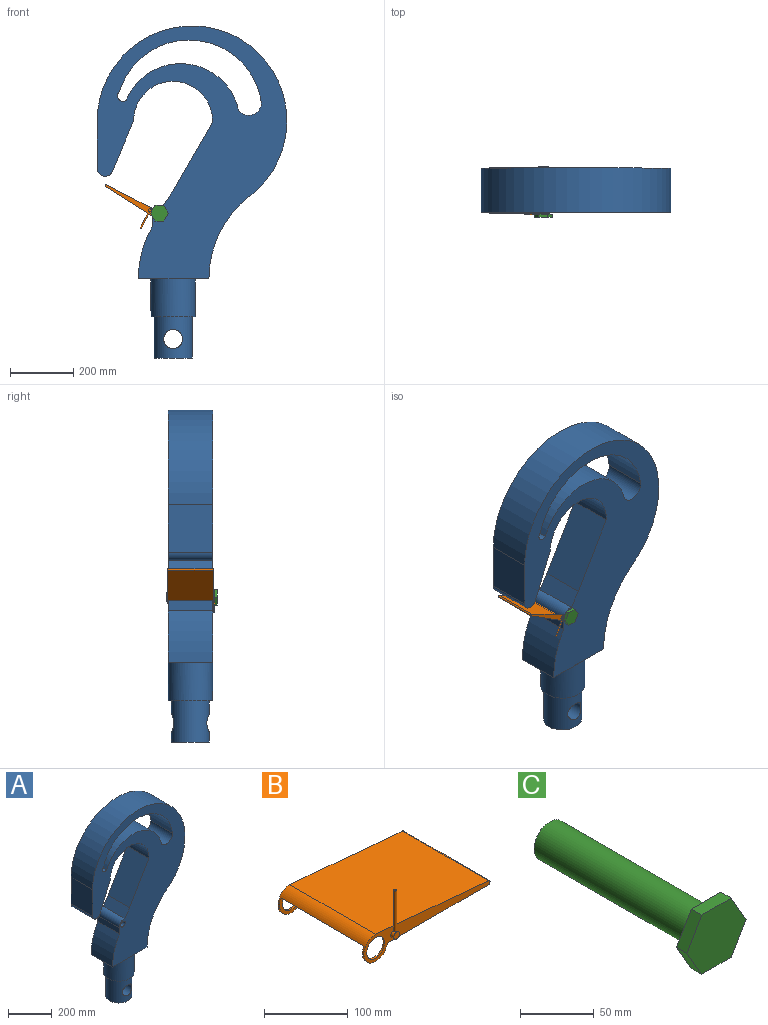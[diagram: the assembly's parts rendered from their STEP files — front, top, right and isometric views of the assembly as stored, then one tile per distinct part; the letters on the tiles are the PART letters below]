
ASSEMBLY  parts=3 mates=2
PART A: 29 faces, bbox 600x140x1050 mm
  f0: plane 800x600mm, normal (0,-1,0), area 214047.9mm2, adj f6,f7,f8,f9,f10,f11,f12,f13
  f1: plane 800x600mm, normal (0,1,0), area 214047.9mm2, adj f6,f7,f8,f9,f10,f11,f12,f13
  f2: cylinder r=60mm len=130mm, axis (0,0,1), area 43158mm2, adj f4,f5,f23
  f3: cylinder r=70mm len=140mm, axis (0,0,1), area 52778.8mm2, adj f4,f6,f7
  f4: plane 140x140mm, normal (0,0,-1), area 4084.1mm2, adj f2,f3
  f5: plane 120x120mm, normal (0,0,-1), area 11309.7mm2, adj f2
  f6: plane 140x110mm, normal (0,0,-1), area 7703.1mm2, adj f0,f1,f3,f17
  f7: plane 140x113.28mm, normal (0,0,-1), area 8161.6mm2, adj f0,f1,f3,f18
  f8: cylinder r=125mm len=140mm, axis (0,1,0), area 24676.8mm2, adj f0,f1,f9,f22
  f9: plane 140x1.56mm, normal (1,0,0), area 218.2mm2, adj f0,f1,f8,f10
  f10: plane 140x40mm, normal (0,0,-1), area 5600mm2, adj f0,f1,f9,f11
  f11: plane 140x1.56mm, normal (-1,0,0), area 218.2mm2, adj f0,f1,f10,f12
  f12: cylinder r=125mm len=140mm, axis (0,1,0), area 25571.4mm2, adj f0,f1,f11,f13
  f13: plane 215.2x140mm, normal (-0.86,0,0.5), area 34830.4mm2, adj f0,f1,f12,f14
  f14: plane 140x45.84mm, normal (-0.82,0,0.57), area 7800mm2, adj f0,f1,f13,f15
  f15: cylinder r=30mm len=140mm, axis (0,1,0), area 8131.9mm2, adj f0,f1,f14,f16
  f16: plane 140x32.55mm, normal (-1,0,0), area 4556.4mm2, adj f0,f1,f15,f17
  f17: cylinder r=330mm len=164.53mm, axis (0,1,0), area 24113.8mm2, adj f0,f1,f6,f16
  f18: cylinder r=330mm len=261.9mm, axis (0,1,0), area 42355.5mm2, adj f0,f1,f7,f19
  f19: cylinder r=300mm len=600mm, axis (0,1,0), area 170451.9mm2, adj f0,f1,f18,f20
  f20: plane 150x140mm, normal (-1,0,0), area 21000mm2, adj f0,f1,f19,f21
  f21: cylinder r=25mm len=140mm, axis (0,1,0), area 9606mm2, adj f0,f1,f20,f22
  f22: plane 159.67x140mm, normal (0.92,0,-0.39), area 24238.6mm2, adj f0,f1,f8,f21
  f23: cylinder r=30mm len=120mm, axis (0,1,0), area 21131.3mm2, adj f2
  f24: cylinder r=15mm len=140mm, axis (0,-1,0), area 13194.7mm2, adj f0,f1
  f25: cylinder r=186.98mm len=355.38mm, axis (0,-1,0), area 66318.4mm2, adj f0,f1,f26,f28
  f26: cylinder r=40mm len=140mm, axis (0,-1,0), area 13981.8mm2, adj f0,f1,f25,f27
  f27: cylinder r=230.77mm len=449.32mm, axis (0,-1,0), area 87399.7mm2, adj f0,f1,f26,f28
  f28: cylinder r=17mm len=140mm, axis (0,-1,0), area 7441.6mm2, adj f0,f1,f25,f27
PART B: 18 faces, bbox 213x150x90 mm
  f0: cylinder r=5mm len=10mm, axis (0,1,0), area 137.5mm2, adj f6,f13,f15,f16
  f1: plane 170.3x145mm, normal (0,0,-1), area 17661.4mm2, adj f3,f4,f6,f7,f10,f11,f12
  f2: cylinder r=15mm len=145mm, axis (0,1,0), area 4003.7mm2, adj f6,f7,f8,f9,f10,f11
  f3: cylinder r=20mm len=145mm, axis (0,1,0), area 3350.9mm2, adj f1,f5,f6,f7,f8,f10,f11
  f4: cylinder r=3mm len=145mm, axis (0,1,0), area 1317.6mm2, adj f1,f5,f6,f7
  f5: plane 190.53x145mm, normal (0.09,0,1), area 27736mm2, adj f3,f4,f6,f7
  f6: plane 213x40mm, normal (0,-1,0), area 2865.1mm2, adj f0,f1,f2,f3,f4,f5
  f7: plane 213x40mm, normal (0,1,0), area 2943.6mm2, adj f1,f2,f3,f4,f5
  f8: plane 140x6.14mm, normal (0,0,-1), area 859.6mm2, adj f2,f3,f10,f11
  f9: plane 140x58.82mm, normal (0,0,-1), area 8234.8mm2, adj f2,f10,f11,f12
  f10: plane 90x30mm, normal (0,-1,0), area 1040.4mm2, adj f1,f2,f3,f8,f9,f12
  f11: plane 90x30mm, normal (0,1,0), area 1040.4mm2, adj f1,f2,f3,f8,f9,f12
  f12: plane 140x13mm, normal (-1,0,0), area 1819.9mm2, adj f1,f9,f10,f11
  f13: plane 10x10mm, normal (0,-1,0), area 78.5mm2, adj f0
  f14: plane 3.5x3.5mm, normal (0,0,-1), area 9.6mm2, adj f15
  f15: cylinder r=1.75mm len=3.5mm, axis (0,0,-1), area 4.5mm2, adj f0,f14
  f16: cylinder r=1.75mm len=60.2mm, axis (0,0,-1), area 658.9mm2, adj f0,f17
  f17: plane 3.5x3.5mm, normal (0,0,1), area 9.6mm2, adj f16
PART C: 10 faces, bbox 56.7x160x49.1 mm
  f0: cylinder r=15mm len=150mm, axis (0,1,0), area 14137.2mm2, adj f1,f9
  f1: plane 30x30mm, normal (0,1,0), area 706.9mm2, adj f0
  f2: plane 28.37x10mm, normal (0,0,1), area 283.7mm2, adj f3,f7,f8,f9
  f3: plane 24.57x14.18mm, normal (-0.87,0,0.5), area 283.7mm2, adj f2,f4,f8,f9
  f4: plane 24.57x14.18mm, normal (-0.87,0,-0.5), area 283.7mm2, adj f3,f5,f8,f9
  f5: plane 28.37x10mm, normal (0,0,-1), area 283.7mm2, adj f4,f6,f8,f9
  f6: plane 24.57x14.18mm, normal (0.87,0,-0.5), area 283.7mm2, adj f5,f7,f8,f9
  f7: plane 24.57x14.18mm, normal (0.87,0,0.5), area 283.7mm2, adj f2,f6,f8,f9
  f8: plane 56.74x49.14mm, normal (0,-1,0), area 2091mm2, adj f2,f3,f4,f5,f6,f7
  f9: plane 56.74x49.14mm, normal (0,1,0), area 1384.2mm2, adj f0,f2,f3,f4,f5,f6,f7
PLACE A t=(-750.94,-82.64,-8.12)mm
PLACE B rot(axis=(0,-1,0),152.7deg) t=(-773.48,-98.6,196)mm
PLACE C t=(-794.43,-82.64,199.66)mm
MATE cylindrical B.f2 <-> A.f24  axis (0,1,0) through (-794.43,-152.64,199.66)mm
MATE pin_slot C.f0 <-> A.f24  axis (0,1,0) through (-794.43,-82.64,199.66)mm
